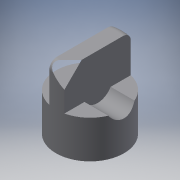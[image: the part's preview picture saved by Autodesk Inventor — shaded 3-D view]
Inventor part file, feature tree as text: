
AUTODESK INVENTOR PART (.ipt)
format: ipt  version: 2016 (Build 200138000, 138)  size: 134,656 bytes
history: native  units: in
note: dims shown in document units (in); Inventor stores cm internally (conversion verified against a paired STEP export)
features: extrude x4, sketch x4, projected_geometry x2, fillet x1
ambient origin geometry x8: Origin, YZ Plane, XZ Plane, XY Plane, X Axis, Y Axis, Z Axis, Center Point
bodies: Solid1 (feature_tree)
feature tree (11):
  extrude  "Extrusion1"  Depth=0.1969in TaperAngle=0.0deg
  extrude  "Extrusion2"  Depth=0.0787in
  extrude  "Extrusion3"  Depth=0.1969in TaperAngle=0.0deg
  fillet  "Fillet1"  Radius=0.0394in
  extrude  "Extrusion7"  Depth=0.0394in
  sketch  "Sketch1"  dims[d0=0.3543in d1=0.1969in d2=0.0in]
  sketch  "Sketch2"  dims[d4=0.0394in d5=0.0787in]
  sketch  "Sketch3"  dims[d6=0.1969in d7=0.0in d8=0.1969in d9=0.0in d14=0.0394in]
  projected_geometry  "Projected Loop1"
  projected_geometry  "Projected Loop2"
  sketch  "Sketch7"  dims[d20=0.0394in d21=0.1575in d22=1.0in d23=0.0in]
